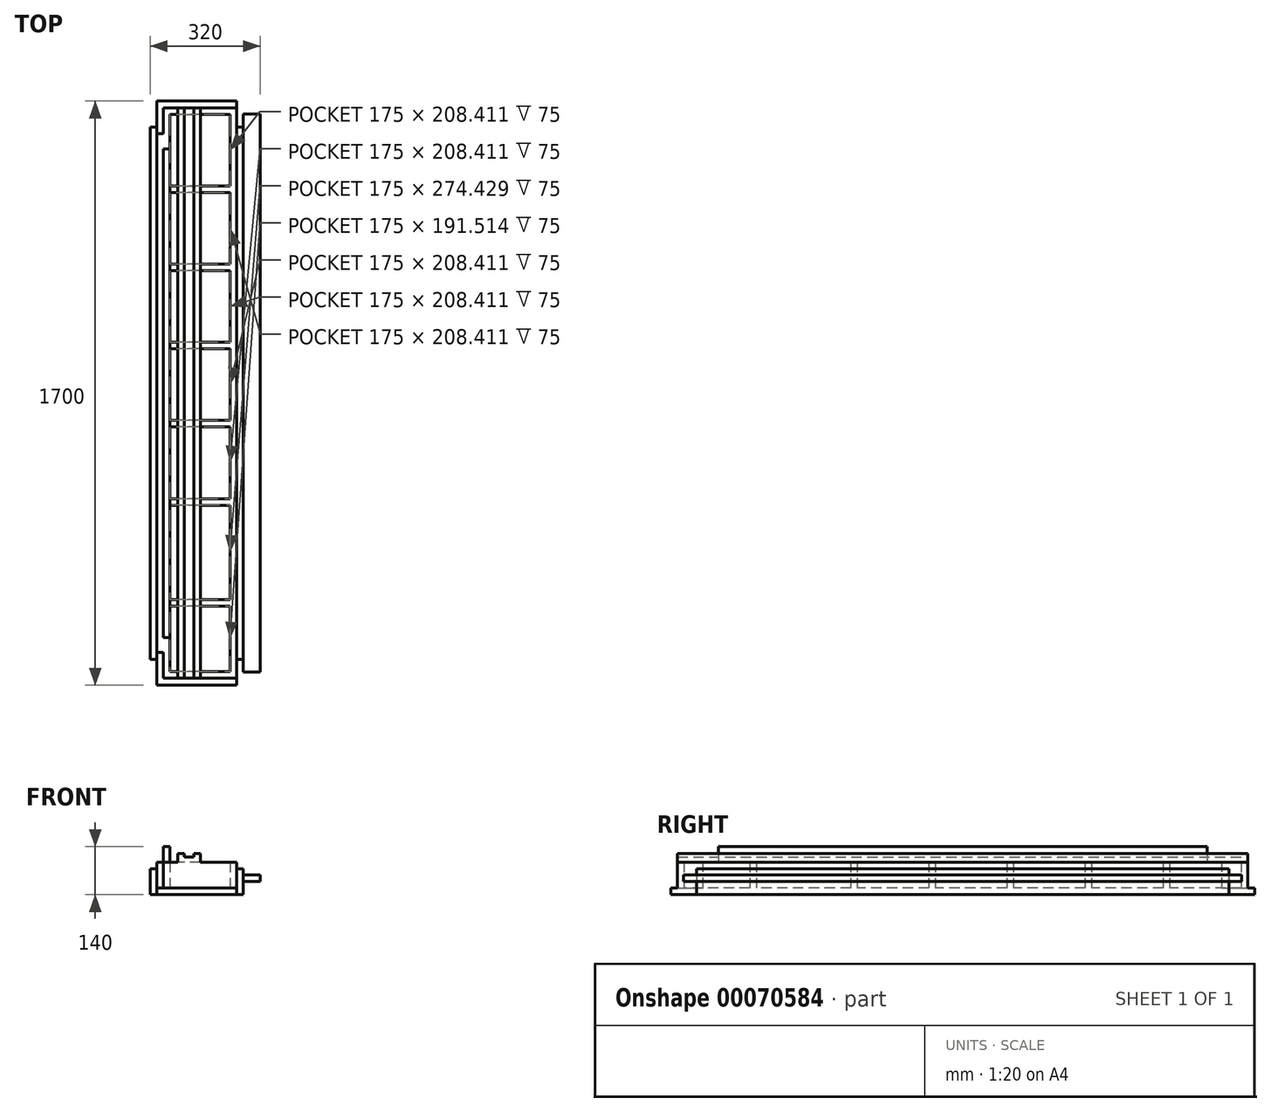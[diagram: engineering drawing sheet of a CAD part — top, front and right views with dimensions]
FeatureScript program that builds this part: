
annotation { "Feature Type Name" : "Feature", "Feature Type Description" : "" }
export const myFeature = defineFeature(function(context is Context, id is Id, definition is map)
    precondition{}
    {
        {
            var Q0;
            Q0=qCreatedBy(makeId("Front.planeOp"),FACE);
            var sketch = newSketch(context, id + "F0", { "sketchPlane" : qUnion([Q0])});
            skLineSegment(sketch, "E0", {"start": v(-19, 0) * mm, "end": v(213, 0) * mm});
            skLineSegment(sketch, "E1", {"start": v(213, 0) * mm, "end": v(213, 75) * mm});
            skLineSegment(sketch, "E2", {"start": v(0, 75) * mm, "end": v(-19, 75) * mm});
            skLineSegment(sketch, "E3", {"start": v(19, 75) * mm, "end": v(213, 75) * mm});
            skLineSegment(sketch, "E4", {"start": v(19, 75) * mm, "end": v(19, 120) * mm});
            skLineSegment(sketch, "E5", {"start": v(19, 120) * mm, "end": v(0, 120) * mm});
            skLineSegment(sketch, "E6", {"start": v(0, 120) * mm, "end": v(0, 75) * mm});
            skLineSegment(sketch, "E7", {"start": v(-19, 75) * mm, "end": v(-19, 0) * mm});
            skSolve(sketch);
        }
        {
            var Q0;
            Q0=makeQuery(id+"F0.imprint","IMPRINT",FACE,{"disambiguationData":[TD([[makeQuery(id+"F0.imprint","IMPRINT",EDGE,{"derivedFrom":sQuery(id+"F0.wireOp",EDGE,"E0")}),1.0]])]});
            extrude(context, id + "F1", {"entities" : qUnion([Q0]), "endBound" : BoundingType.SYMMETRIC, "depth" : 1660 * mm});
        }
        {
            var Q0;
            Q0=qCreatedBy(makeId("Top.planeOp"),FACE);
            cPlane(context, id + "F2", {"entities" : qUnion([Q0]), "cplaneType" : CPlaneType.OFFSET, "offset" : 19 * mm, "width" : 150 * mm, "height" : 150 * mm});
        }
        {
            var Q0;
            Q0=qCreatedBy(id+"F2.planeOp",FACE);
            var sketch = newSketch(context, id + "F3", { "sketchPlane" : qUnion([Q0])});
            skLineSegment(sketch, "E8.bottom", {"start": v(19, 811) * mm, "end": v(194, 811) * mm});
            skLineSegment(sketch, "E8.top", {"start": v(19, 602.59) * mm, "end": v(194, 602.59) * mm});
            skLineSegment(sketch, "E8.left", {"start": v(19, 811) * mm, "end": v(19, 602.59) * mm});
            skLineSegment(sketch, "E8.right", {"start": v(194, 811) * mm, "end": v(194, 602.59) * mm});
            skLineSegment(sketch, "E9.bottom", {"start": v(19, 583.59) * mm, "end": v(194, 583.59) * mm});
            skLineSegment(sketch, "E9.top", {"start": v(19, 375.18) * mm, "end": v(194, 375.18) * mm});
            skLineSegment(sketch, "E9.left", {"start": v(19, 583.59) * mm, "end": v(19, 375.18) * mm});
            skLineSegment(sketch, "E9.right", {"start": v(194, 583.59) * mm, "end": v(194, 375.18) * mm});
            skLineSegment(sketch, "E10.bottom", {"start": v(19, 356.18) * mm, "end": v(194, 356.18) * mm});
            skLineSegment(sketch, "E10.top", {"start": v(19, 147.77) * mm, "end": v(194, 147.77) * mm});
            skLineSegment(sketch, "E10.left", {"start": v(19, 356.18) * mm, "end": v(19, 147.77) * mm});
            skLineSegment(sketch, "E10.right", {"start": v(194, 356.18) * mm, "end": v(194, 147.77) * mm});
            skLineSegment(sketch, "E11.bottom", {"start": v(19, 128.77) * mm, "end": v(194, 128.77) * mm});
            skLineSegment(sketch, "E11.top", {"start": v(19, -79.64) * mm, "end": v(194, -79.64) * mm});
            skLineSegment(sketch, "E11.left", {"start": v(19, 128.77) * mm, "end": v(19, -79.64) * mm});
            skLineSegment(sketch, "E11.right", {"start": v(194, 128.77) * mm, "end": v(194, -79.64) * mm});
            skLineSegment(sketch, "E12.bottom", {"start": v(19, -619.49) * mm, "end": v(194, -619.49) * mm});
            skLineSegment(sketch, "E12.top", {"start": v(19, -811) * mm, "end": v(194, -811) * mm});
            skLineSegment(sketch, "E12.left", {"start": v(19, -619.49) * mm, "end": v(19, -811) * mm});
            skLineSegment(sketch, "E12.right", {"start": v(194, -619.49) * mm, "end": v(194, -811) * mm});
            skLineSegment(sketch, "E13.bottom", {"start": v(19, -326.06) * mm, "end": v(194, -326.06) * mm});
            skLineSegment(sketch, "E13.top", {"start": v(19, -600.49) * mm, "end": v(194, -600.49) * mm});
            skLineSegment(sketch, "E13.left", {"start": v(19, -326.06) * mm, "end": v(19, -600.49) * mm});
            skLineSegment(sketch, "E13.right", {"start": v(194, -326.06) * mm, "end": v(194, -600.49) * mm});
            skLineSegment(sketch, "E14.bottom", {"start": v(19, -98.64) * mm, "end": v(194, -98.64) * mm});
            skLineSegment(sketch, "E14.top", {"start": v(19, -307.06) * mm, "end": v(194, -307.06) * mm});
            skLineSegment(sketch, "E14.left", {"start": v(19, -98.64) * mm, "end": v(19, -307.06) * mm});
            skLineSegment(sketch, "E14.right", {"start": v(194, -98.64) * mm, "end": v(194, -307.06) * mm});
            skSolve(sketch);
        }
        {
            var Q0;
            Q0=qSketchRegion(id+"F3",true);
            extrude(context, id + "F4", {"entities" : qUnion([Q0]), "operationType" : NewBodyOperationType.REMOVE, "depth" : 100 * mm});
        }
        {
            var Q0;
            Q0=makeQuery(id+"F1.opExtrude","SWEPT_FACE",FACE,{"disambiguationData":[OSD([sQuery(id+"F0.wireOp",EDGE,"E3")])]});
            var sketch = newSketch(context, id + "F5", { "sketchPlane" : qUnion([Q0])});
            skLineSegment(sketch, "E15.bottom", {"start": v(42, 830) * mm, "end": v(108, 830) * mm});
            skLineSegment(sketch, "E15.top", {"start": v(42, -830) * mm, "end": v(108, -830) * mm});
            skLineSegment(sketch, "E15.left", {"start": v(42, 830) * mm, "end": v(42, -830) * mm});
            skLineSegment(sketch, "E15.right", {"start": v(108, 830) * mm, "end": v(108, -830) * mm});
            skSolve(sketch);
        }
        {
            var Q0;
            Q0=qSketchRegion(id+"F5",true);
            extrude(context, id + "F6", {"entities" : qUnion([Q0]), "operationType" : NewBodyOperationType.ADD, "depth" : 25 * mm});
        }
        {
            var Q0;
            Q0=qCreatedBy(makeId("Front.planeOp"),FACE);
            var sketch = newSketch(context, id + "F7", { "sketchPlane" : qUnion([Q0])});
            skLineSegment(sketch, "E16", {"start": v(-19, 56) * mm, "end": v(-38, 56) * mm});
            skLineSegment(sketch, "E17", {"start": v(-38, 56) * mm, "end": v(-38, -19) * mm});
            skLineSegment(sketch, "E18", {"start": v(-38, -19) * mm, "end": v(232, -19) * mm});
            skLineSegment(sketch, "E19", {"start": v(232, -19) * mm, "end": v(232, 56) * mm});
            skLineSegment(sketch, "E20", {"start": v(232, 56) * mm, "end": v(213, 56) * mm});
            skLineSegment(sketch, "E21", {"start": v(213, 56) * mm, "end": v(213, 0) * mm});
            skLineSegment(sketch, "E22", {"start": v(213, 0) * mm, "end": v(-19, 0) * mm});
            skLineSegment(sketch, "E23", {"start": v(-19, 0) * mm, "end": v(-19, 56) * mm});
            skSolve(sketch);
        }
        {
            var Q0;
            Q0 = qSketchRegion(id + "F7", true);
            extrude(context, id + "F8", {"entities" : qUnion([Q0]), "operationType" : NewBodyOperationType.ADD, "endBound" : BoundingType.SYMMETRIC, "depth" : 1700 * mm});
        }
        {
            var Q0;
            Q0=makeQuery(id+"F8.opExtrude","SWEPT_FACE",FACE,{"disambiguationData":[OSD([sQuery(id+"F7.wireOp",EDGE,"E17")])]});
            var sketch = newSketch(context, id + "F9", { "sketchPlane" : qUnion([Q0])});
            skLineSegment(sketch, "E24.bottom", {"start": v(-897.86, -54) * mm, "end": v(-775, -54) * mm});
            skLineSegment(sketch, "E24.top", {"start": v(-897.86, 112.59) * mm, "end": v(-775, 112.59) * mm});
            skLineSegment(sketch, "E24.left", {"start": v(-775, -54) * mm, "end": v(-775, 112.59) * mm});
            skLineSegment(sketch, "E24.right", {"start": v(-897.86, -54) * mm, "end": v(-897.86, 112.59) * mm});
            skLineSegment(sketch, "E25.bottom", {"start": v(775, 157.36) * mm, "end": v(896.81, 157.36) * mm});
            skLineSegment(sketch, "E25.top", {"start": v(775, -68.57) * mm, "end": v(896.81, -68.57) * mm});
            skLineSegment(sketch, "E25.left", {"start": v(775, 157.36) * mm, "end": v(775, -68.57) * mm});
            skLineSegment(sketch, "E25.right", {"start": v(896.81, 157.36) * mm, "end": v(896.81, -68.57) * mm});
            skSolve(sketch);
        }
        {
            var Q0;
            Q0 = qSketchRegion(id + "F9", true);
            extrude(context, id + "F10", {"entities" : qUnion([Q0]), "operationType" : NewBodyOperationType.REMOVE, "oppositeDirection" : true, "depth" : 19 * mm});
        }
        {
            var Q0;
            Q0=makeQuery(id+"F8.opExtrude","SWEPT_FACE",FACE,{"disambiguationData":[OSD([sQuery(id+"F7.wireOp",EDGE,"E19")])]});
            var sketch = newSketch(context, id + "F11", { "sketchPlane" : qUnion([Q0])});
            skLineSegment(sketch, "E26.bottom", {"start": v(-887.34, 89.13) * mm, "end": v(-775, 89.13) * mm});
            skLineSegment(sketch, "E26.top", {"start": v(-887.34, -58.74) * mm, "end": v(-775, -58.74) * mm});
            skLineSegment(sketch, "E26.left", {"start": v(-887.34, 89.13) * mm, "end": v(-887.34, -58.74) * mm});
            skLineSegment(sketch, "E26.right", {"start": v(-775, 89.13) * mm, "end": v(-775, -58.74) * mm});
            skLineSegment(sketch, "E27.bottom", {"start": v(775, 199.4) * mm, "end": v(1127.19, 199.4) * mm});
            skLineSegment(sketch, "E27.top", {"start": v(775, -191.73) * mm, "end": v(1127.19, -191.73) * mm});
            skLineSegment(sketch, "E27.left", {"start": v(775, 199.4) * mm, "end": v(775, -191.73) * mm});
            skLineSegment(sketch, "E27.right", {"start": v(1127.19, 199.4) * mm, "end": v(1127.19, -191.73) * mm});
            skSolve(sketch);
        }
        {
            var Q0;
            Q0 = qSketchRegion(id + "F11", true);
            extrude(context, id + "F12", {"entities" : qUnion([Q0]), "operationType" : NewBodyOperationType.REMOVE, "oppositeDirection" : true, "depth" : 19 * mm});
        }
        {
            var Q0;
            Q0=makeQuery(id+"F1.opExtrude","SWEPT_FACE",FACE,{"disambiguationData":[OSD([sQuery(id+"F0.wireOp",EDGE,"E6")])]});
            var sketch = newSketch(context, id + "F13", { "sketchPlane" : qUnion([Q0])});
            skLineSegment(sketch, "E28.bottom", {"start": v(-918.22, 141.81) * mm, "end": v(-711, 141.81) * mm});
            skLineSegment(sketch, "E28.top", {"start": v(-918.22, 75) * mm, "end": v(-711, 75) * mm});
            skLineSegment(sketch, "E28.left", {"start": v(-918.22, 141.81) * mm, "end": v(-918.22, 75) * mm});
            skLineSegment(sketch, "E28.right", {"start": v(-711, 141.81) * mm, "end": v(-711, 75) * mm});
            skLineSegment(sketch, "E29.bottom", {"start": v(916.5, 146.95) * mm, "end": v(711, 146.95) * mm});
            skLineSegment(sketch, "E29.top", {"start": v(916.5, 75) * mm, "end": v(711, 75) * mm});
            skLineSegment(sketch, "E29.left", {"start": v(916.5, 146.95) * mm, "end": v(916.5, 75) * mm});
            skLineSegment(sketch, "E29.right", {"start": v(711, 146.95) * mm, "end": v(711, 75) * mm});
            skSolve(sketch);
        }
        {
            var Q0;
            Q0 = qSketchRegion(id + "F13", true);
            extrude(context, id + "F14", {"entities" : qUnion([Q0]), "operationType" : NewBodyOperationType.REMOVE, "oppositeDirection" : true, "depth" : 25 * mm});
        }
        {
            var Q0;
            Q0=makeQuery(id+"F8.opExtrude","SWEPT_FACE",FACE,{"disambiguationData":[OSD([sQuery(id+"F7.wireOp",EDGE,"E19")])]});
            var sketch = newSketch(context, id + "F15", { "sketchPlane" : qUnion([Q0])});
            skPoint(sketch, "E30.oppositeSnap0", {"position": v(787.5, 19) * mm});
            skLineSegment(sketch, "E30.bottom", {"start": v(-812, 38) * mm, "end": v(812, 38) * mm});
            skLineSegment(sketch, "E30.top", {"start": v(-812, 19) * mm, "end": v(812, 19) * mm});
            skLineSegment(sketch, "E30.left", {"start": v(-812, 38) * mm, "end": v(-812, 19) * mm});
            skLineSegment(sketch, "E30.right", {"start": v(812, 38) * mm, "end": v(812, 19) * mm});
            skSolve(sketch);
        }
        {
            var Q0;
            Q0 = qSketchRegion(id + "F15", true);
            extrude(context, id + "F16", {"entities" : qUnion([Q0]), "operationType" : NewBodyOperationType.ADD, "depth" : 50 * mm});
        }
        {
            var Q0;
            Q0=makeQuery(id+"F10.boolean.opBoolean","MERGE",FACE,{"derivedFrom":[makeQuery(id+"F1.opExtrude","SWEPT_FACE",FACE,{"disambiguationData":[OSD([sQuery(id+"F0.wireOp",EDGE,"E7")])]}),makeQuery(id+"F10.opExtrude","CAP_FACE",FACE,{"disambiguationData":[OSD([sQuery(id+"F9.wireOp",EDGE,"E24.bottom"),sQuery(id+"F9.wireOp",EDGE,"E24.top"),sQuery(id+"F9.wireOp",EDGE,"E24.left"),sQuery(id+"F9.wireOp",EDGE,"E24.right")])],"isStart":false}),makeQuery(id+"F10.opExtrude","CAP_FACE",FACE,{"disambiguationData":[OSD([sQuery(id+"F9.wireOp",EDGE,"E25.bottom"),sQuery(id+"F9.wireOp",EDGE,"E25.top"),sQuery(id+"F9.wireOp",EDGE,"E25.left"),sQuery(id+"F9.wireOp",EDGE,"E25.right")])],"isStart":false})]});
            var sketch = newSketch(context, id + "F17", { "sketchPlane" : qUnion([Q0])});
            skLineSegment(sketch, "E31.bottom", {"start": v(-850, 0) * mm, "end": v(-755, 0) * mm});
            skLineSegment(sketch, "E31.left", {"start": v(-850, 0) * mm, "end": v(-850, 136.2) * mm});
            skLineSegment(sketch, "E32", {"start": v(-755, 0) * mm, "end": v(-755, 136.46) * mm});
            skLineSegment(sketch, "E33", {"start": v(-755, 136.46) * mm, "end": v(-850, 136.2) * mm});
            skLineSegment(sketch, "E34.bottom", {"start": v(850, 0) * mm, "end": v(755, 0) * mm});
            skLineSegment(sketch, "E34.top", {"start": v(850, 152.76) * mm, "end": v(755, 152.76) * mm});
            skLineSegment(sketch, "E34.left", {"start": v(850, 0) * mm, "end": v(850, 152.76) * mm});
            skLineSegment(sketch, "E34.right", {"start": v(755, 0) * mm, "end": v(755, 152.76) * mm});
            skSolve(sketch);
        }
        {
            var Q0;
            Q0 = qSketchRegion(id + "F17", true);
            extrude(context, id + "F18", {"entities" : qUnion([Q0]), "operationType" : NewBodyOperationType.REMOVE, "oppositeDirection" : true, "depth" : 19 * mm});
        }
        {
            var Q0;
            Q0=makeQuery(id+"F4.boolean.opBoolean","COPY",FACE,{"derivedFrom":makeQuery(id+"F4.opExtrude","CAP_FACE",FACE,{"disambiguationData":[OSD([sQuery(id+"F3.wireOp",EDGE,"E8.bottom"),sQuery(id+"F3.wireOp",EDGE,"E8.top"),sQuery(id+"F3.wireOp",EDGE,"E8.left"),sQuery(id+"F3.wireOp",EDGE,"E8.right")])],"isStart":true})});
            var sketch = newSketch(context, id + "F19", { "sketchPlane" : qUnion([Q0])});
            skLineSegment(sketch, "E35.left", {"start": v(194, 811) * mm, "end": v(194, 602.59) * mm});
            skLineSegment(sketch, "E36.bottom", {"start": v(19, 811) * mm, "end": v(194, 811) * mm});
            skLineSegment(sketch, "E36.top", {"start": v(19, 602.59) * mm, "end": v(194, 602.59) * mm});
            skLineSegment(sketch, "E36.left", {"start": v(19, 811) * mm, "end": v(19, 602.59) * mm});
            skLineSegment(sketch, "E37.bottom", {"start": v(194, 583.59) * mm, "end": v(19, 583.59) * mm});
            skLineSegment(sketch, "E37.top", {"start": v(194, 375.18) * mm, "end": v(19, 375.18) * mm});
            skLineSegment(sketch, "E37.left", {"start": v(194, 583.59) * mm, "end": v(194, 375.18) * mm});
            skLineSegment(sketch, "E37.right", {"start": v(19, 583.59) * mm, "end": v(19, 375.18) * mm});
            skLineSegment(sketch, "E38.bottom", {"start": v(194, 356.18) * mm, "end": v(19, 356.18) * mm});
            skLineSegment(sketch, "E38.top", {"start": v(194, 147.77) * mm, "end": v(19, 147.77) * mm});
            skLineSegment(sketch, "E38.left", {"start": v(194, 356.18) * mm, "end": v(194, 147.77) * mm});
            skLineSegment(sketch, "E38.right", {"start": v(19, 356.18) * mm, "end": v(19, 147.77) * mm});
            skLineSegment(sketch, "E39.bottom", {"start": v(194, 128.77) * mm, "end": v(19, 128.77) * mm});
            skLineSegment(sketch, "E39.top", {"start": v(194, -79.64) * mm, "end": v(19, -79.64) * mm});
            skLineSegment(sketch, "E39.left", {"start": v(194, 128.77) * mm, "end": v(194, -79.64) * mm});
            skLineSegment(sketch, "E39.right", {"start": v(19, 128.77) * mm, "end": v(19, -79.64) * mm});
            skLineSegment(sketch, "E40.bottom", {"start": v(194, -98.64) * mm, "end": v(19, -98.64) * mm});
            skLineSegment(sketch, "E40.top", {"start": v(194, -307.06) * mm, "end": v(19, -307.06) * mm});
            skLineSegment(sketch, "E40.left", {"start": v(194, -98.64) * mm, "end": v(194, -307.06) * mm});
            skLineSegment(sketch, "E40.right", {"start": v(19, -98.64) * mm, "end": v(19, -307.06) * mm});
            skLineSegment(sketch, "E41.bottom", {"start": v(194, -326.06) * mm, "end": v(19, -326.06) * mm});
            skLineSegment(sketch, "E41.top", {"start": v(194, -600.49) * mm, "end": v(19, -600.49) * mm});
            skLineSegment(sketch, "E41.left", {"start": v(194, -326.06) * mm, "end": v(194, -600.49) * mm});
            skLineSegment(sketch, "E41.right", {"start": v(19, -326.06) * mm, "end": v(19, -600.49) * mm});
            skLineSegment(sketch, "E42.bottom", {"start": v(194, -619.49) * mm, "end": v(19, -619.49) * mm});
            skLineSegment(sketch, "E42.top", {"start": v(194, -811) * mm, "end": v(19, -811) * mm});
            skLineSegment(sketch, "E42.left", {"start": v(194, -619.49) * mm, "end": v(194, -811) * mm});
            skLineSegment(sketch, "E42.right", {"start": v(19, -619.49) * mm, "end": v(19, -811) * mm});
            skSolve(sketch);
        }
        {
            var Q0;
            Q0 = qSketchRegion(id + "F19", true);
            extrude(context, id + "F20", {"entities" : qUnion([Q0]), "operationType" : NewBodyOperationType.REMOVE, "oppositeDirection" : true, "depth" : 19 * mm});
        }
        {
            var Q0;
            Q0=makeQuery(id+"F8.opExtrude","SWEPT_FACE",FACE,{"disambiguationData":[OSD([sQuery(id+"F7.wireOp",EDGE,"E18")])]});
            var sketch = newSketch(context, id + "F21", { "sketchPlane" : qUnion([Q0])});
            skLineSegment(sketch, "E43.bottom", {"start": v(213, 775) * mm, "end": v(212, 775) * mm});
            skLineSegment(sketch, "E43.top", {"start": v(213, -775) * mm, "end": v(212, -775) * mm});
            skLineSegment(sketch, "E43.left", {"start": v(213, 775) * mm, "end": v(213, -775) * mm});
            skLineSegment(sketch, "E43.right", {"start": v(212, 775) * mm, "end": v(212, -775) * mm});
            skLineSegment(sketch, "E44.bottom", {"start": v(-19, 775) * mm, "end": v(-18, 775) * mm});
            skLineSegment(sketch, "E44.top", {"start": v(-19, -775) * mm, "end": v(-18, -775) * mm});
            skLineSegment(sketch, "E44.left", {"start": v(-19, 775) * mm, "end": v(-19, -775) * mm});
            skLineSegment(sketch, "E44.right", {"start": v(-18, 775) * mm, "end": v(-18, -775) * mm});
            skSolve(sketch);
        }
        {
            var Q0;
            Q0 = qSketchRegion(id + "F21", true);
            extrude(context, id + "F22", {"entities" : qUnion([Q0]), "operationType" : NewBodyOperationType.ADD, "depth" : 1 * mm});
        }
        {
            var Q0;
            Q0=makeQuery(id+"F6.boolean.opBoolean","MERGE",FACE,{"derivedFrom":[makeQuery(id+"F1.opExtrude","CAP_FACE",FACE,{"disambiguationData":[OSD([sQuery(id+"F0.wireOp",EDGE,"E0"),sQuery(id+"F0.wireOp",EDGE,"E1"),sQuery(id+"F0.wireOp",EDGE,"E2"),sQuery(id+"F0.wireOp",EDGE,"E3"),sQuery(id+"F0.wireOp",EDGE,"E4"),sQuery(id+"F0.wireOp",EDGE,"E5"),sQuery(id+"F0.wireOp",EDGE,"E6"),sQuery(id+"F0.wireOp",EDGE,"E7")])],"isStart":true}),makeQuery(id+"F6.opExtrude","SWEPT_FACE",FACE,{"disambiguationData":[OSD([sQuery(id+"F5.wireOp",EDGE,"E15.bottom")])]})]});
            var sketch = newSketch(context, id + "F23", { "sketchPlane" : qUnion([Q0])});
            skLineSegment(sketch, "E45.bottom", {"start": v(-89, 100) * mm, "end": v(-61, 100) * mm});
            skLineSegment(sketch, "E45.top", {"start": v(-89, 90) * mm, "end": v(-61, 90) * mm});
            skLineSegment(sketch, "E45.left", {"start": v(-89, 100) * mm, "end": v(-89, 90) * mm});
            skLineSegment(sketch, "E45.right", {"start": v(-61, 100) * mm, "end": v(-61, 90) * mm});
            skSolve(sketch);
        }
        {
            var Q0;
            Q0 = qSketchRegion(id + "F23", true);
            extrude(context, id + "F24", {"entities" : qUnion([Q0]), "operationType" : NewBodyOperationType.REMOVE, "oppositeDirection" : true, "depth" : 2000 * mm});
        }
    });
